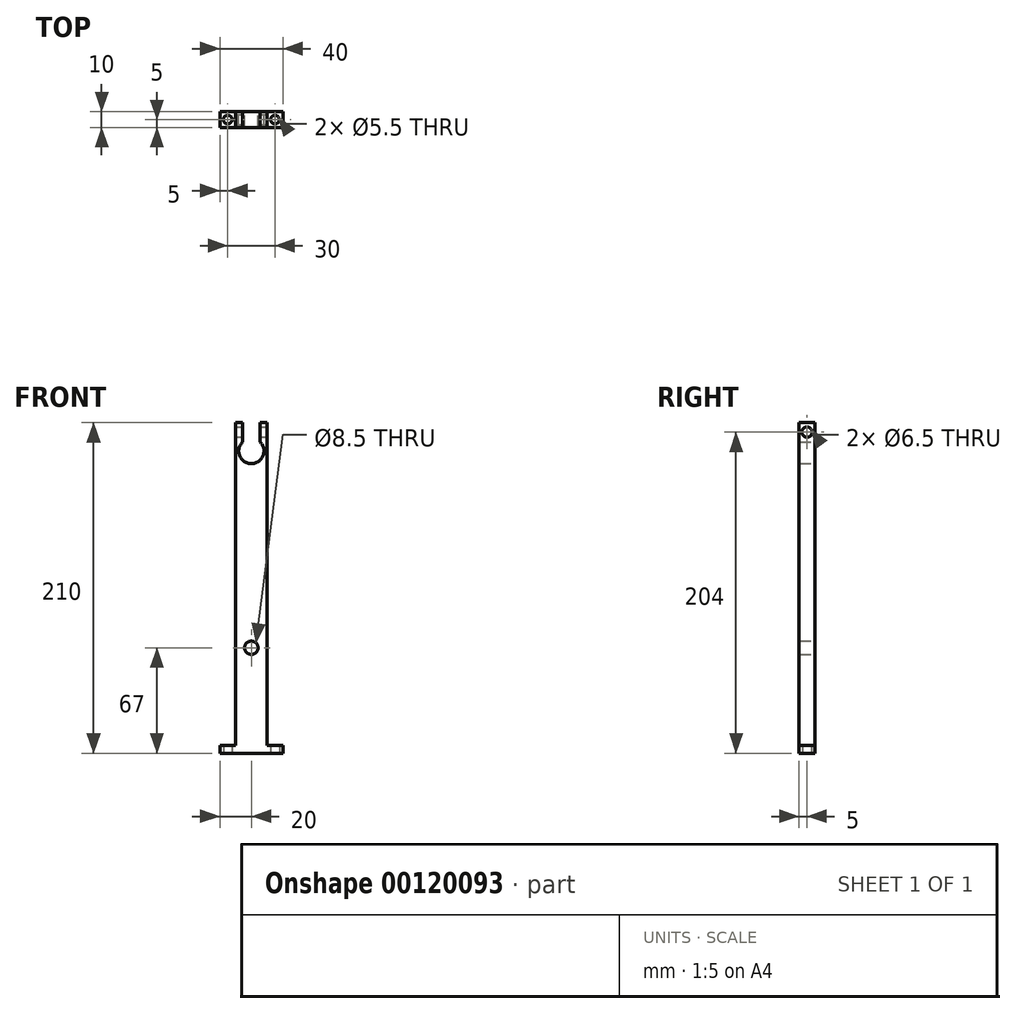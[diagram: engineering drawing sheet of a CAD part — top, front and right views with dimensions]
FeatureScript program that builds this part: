
annotation { "Feature Type Name" : "Feature", "Feature Type Description" : "" }
export const myFeature = defineFeature(function(context is Context, id is Id, definition is map)
    precondition{}
    {
        {
            var Q0;
            Q0=qCreatedBy(makeId("Front.planeOp"),FACE);
            var sketch = newSketch(context, id + "F0", { "sketchPlane" : qUnion([Q0])});
            skLineSegment(sketch, "E0.bottom", {"start": v(-10, -105) * mm, "end": v(10, -105) * mm});
            skLineSegment(sketch, "E0.top", {"start": v(-10, 105) * mm, "end": v(10, 105) * mm});
            skLineSegment(sketch, "E0.left", {"start": v(-10, -105) * mm, "end": v(-10, 105) * mm});
            skLineSegment(sketch, "E0.right", {"start": v(10, -105) * mm, "end": v(10, 105) * mm});
            skPoint(sketch, "E0.middle", {"position": v(0, 0) * mm});
            skLineSegment(sketch, "E1", {"start": v(0, 105) * mm, "end": v(0, 87) * mm});
            skPoint(sketch, "E1.endSnap0", {"position": v(0, 105) * mm});
            skCircle(sketch, "E2", {"center": v(0, 87) * mm, "radius": 8 * mm});
            skLineSegment(sketch, "E3", {"start": v(0, 87) * mm, "end": v(-5.5, 87) * mm});
            skLineSegment(sketch, "E4", {"start": v(-5.5, 87) * mm, "end": v(5.5, 87) * mm});
            skLineSegment(sketch, "E5", {"start": v(5.5, 87) * mm, "end": v(5.5, 105) * mm});
            skLineSegment(sketch, "E6", {"start": v(-5.5, 87) * mm, "end": v(-5.5, 105) * mm});
            skLineSegment(sketch, "E7", {"start": v(0, 87) * mm, "end": v(0, -38) * mm});
            skCircle(sketch, "E8", {"center": v(0, -38) * mm, "radius": 4.25 * mm});
            skSolve(sketch);
        }
        {
            var Q0;
            Q0=makeQuery(id+"F0.imprint","IMPRINT",FACE,{"disambiguationData":[TD([[makeQuery(id+"F0.imprint","IMPRINT",EDGE,{"derivedFrom":sQuery(id+"F0.wireOp",EDGE,"E0.bottom")}),1.0]])]});
            extrude(context, id + "F1", {"entities" : qUnion([Q0]), "endBound" : BoundingType.SYMMETRIC, "depth" : 10 * mm});
        }
        {
            var Q0;
            Q0=makeQuery(id+"F1.opExtrude","SWEPT_FACE",FACE,{"disambiguationData":[OSD([sQuery(id+"F0.wireOp",EDGE,"E0.right")])]});
            var sketch = newSketch(context, id + "F2", { "sketchPlane" : qUnion([Q0])});
            skLineSegment(sketch, "E9", {"start": v(0, 105) * mm, "end": v(0, 99) * mm});
            skCircle(sketch, "E10", {"center": v(0, 99) * mm, "radius": 3.25 * mm});
            skSolve(sketch);
        }
        {
            var Q0;
            Q0 = qSketchRegion(id + "F2", true);
            extrude(context, id + "F3", {"entities" : qUnion([Q0]), "operationType" : NewBodyOperationType.REMOVE, "oppositeDirection" : true, "depth" : 25 * mm});
        }
        {
            var Q0;
            Q0=makeQuery(id+"F1.opExtrude","SWEPT_FACE",FACE,{"disambiguationData":[OSD([sQuery(id+"F0.wireOp",EDGE,"E0.bottom")])]});
            var sketch = newSketch(context, id + "F4", { "sketchPlane" : qUnion([Q0])});
            skLineSegment(sketch, "E11.bottom", {"start": v(-10, 5) * mm, "end": v(-20, 5) * mm});
            skLineSegment(sketch, "E11.top", {"start": v(-10, -5) * mm, "end": v(-20, -5) * mm});
            skLineSegment(sketch, "E11.left", {"start": v(-10, 5) * mm, "end": v(-10, -5) * mm});
            skLineSegment(sketch, "E11.right", {"start": v(-20, 5) * mm, "end": v(-20, -5) * mm});
            skLineSegment(sketch, "E12.bottom", {"start": v(10, 5) * mm, "end": v(20, 5) * mm});
            skLineSegment(sketch, "E12.top", {"start": v(10, -5) * mm, "end": v(20, -5) * mm});
            skLineSegment(sketch, "E12.left", {"start": v(10, 5) * mm, "end": v(10, -5) * mm});
            skLineSegment(sketch, "E12.right", {"start": v(20, 5) * mm, "end": v(20, -5) * mm});
            skLineSegment(sketch, "E13", {"start": v(15, 5) * mm, "end": v(15, 0) * mm});
            skLineSegment(sketch, "E14", {"start": v(-15, 5) * mm, "end": v(-15, 0) * mm});
            skCircle(sketch, "E15", {"center": v(-15, 0) * mm, "radius": 2.75 * mm});
            skCircle(sketch, "E16", {"center": v(15, 0) * mm, "radius": 2.75 * mm});
            skSolve(sketch);
        }
        {
            var Q0;
            Q0 = qSketchRegion(id + "F4", true);
            extrude(context, id + "F5", {"entities" : qUnion([Q0]), "operationType" : NewBodyOperationType.ADD, "oppositeDirection" : true, "depth" : 5 * mm});
        }
    });
